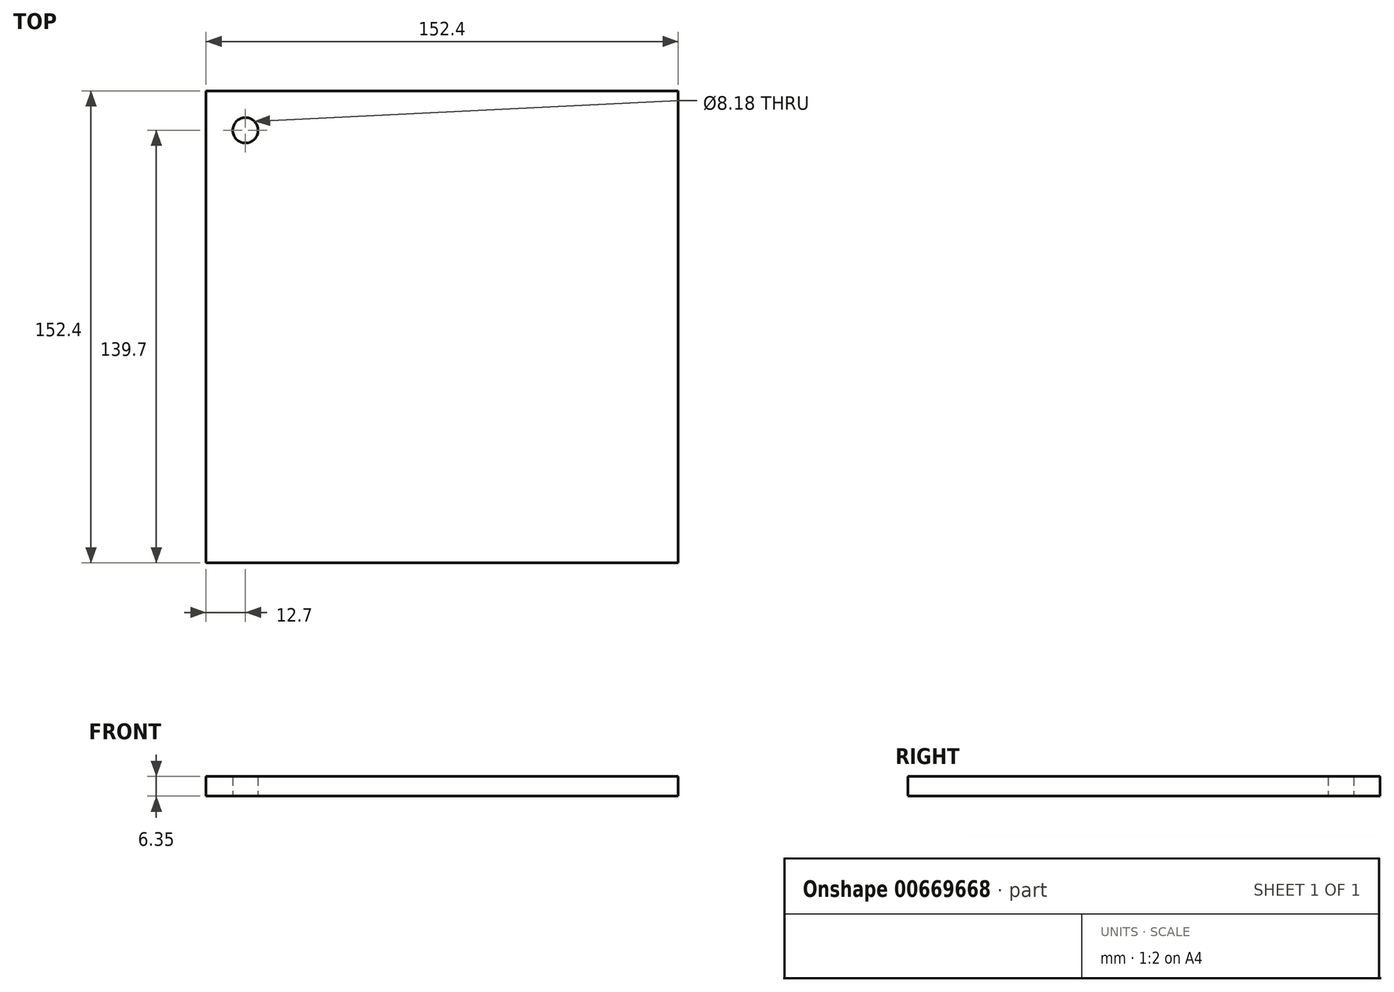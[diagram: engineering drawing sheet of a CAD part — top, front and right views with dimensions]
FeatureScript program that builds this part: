
annotation { "Feature Type Name" : "Feature", "Feature Type Description" : "" }
export const myFeature = defineFeature(function(context is Context, id is Id, definition is map)
    precondition{}
    {
        {
            var Q0;
            Q0=qCreatedBy(makeId("Top.planeOp"),FACE);
            var sketch = newSketch(context, id + "F0", { "sketchPlane" : qUnion([Q0])});
            skLineSegment(sketch, "E0.bottom", {"start": v(76.2, 76.2) * mm, "end": v(-76.2, 76.2) * mm});
            skLineSegment(sketch, "E0.top", {"start": v(76.2, -76.2) * mm, "end": v(-76.2, -76.2) * mm});
            skLineSegment(sketch, "E0.left", {"start": v(76.2, 76.2) * mm, "end": v(76.2, -76.2) * mm});
            skLineSegment(sketch, "E0.right", {"start": v(-76.2, 76.2) * mm, "end": v(-76.2, -76.2) * mm});
            skPoint(sketch, "E0.middle", {"position": v(0, 0) * mm});
            skCircle(sketch, "E1", {"center": v(-63.5, 63.5) * mm, "radius": 4.09 * mm});
            skSolve(sketch);
        }
        {
            var Q0;
            Q0 = qSketchRegion(id + "F0", true);
            extrude(context, id + "F1", {"entities" : qUnion([Q0]), "depth" : 6.35 * mm, "offsetDistance" : 25.4 * mm});
        }
    });
